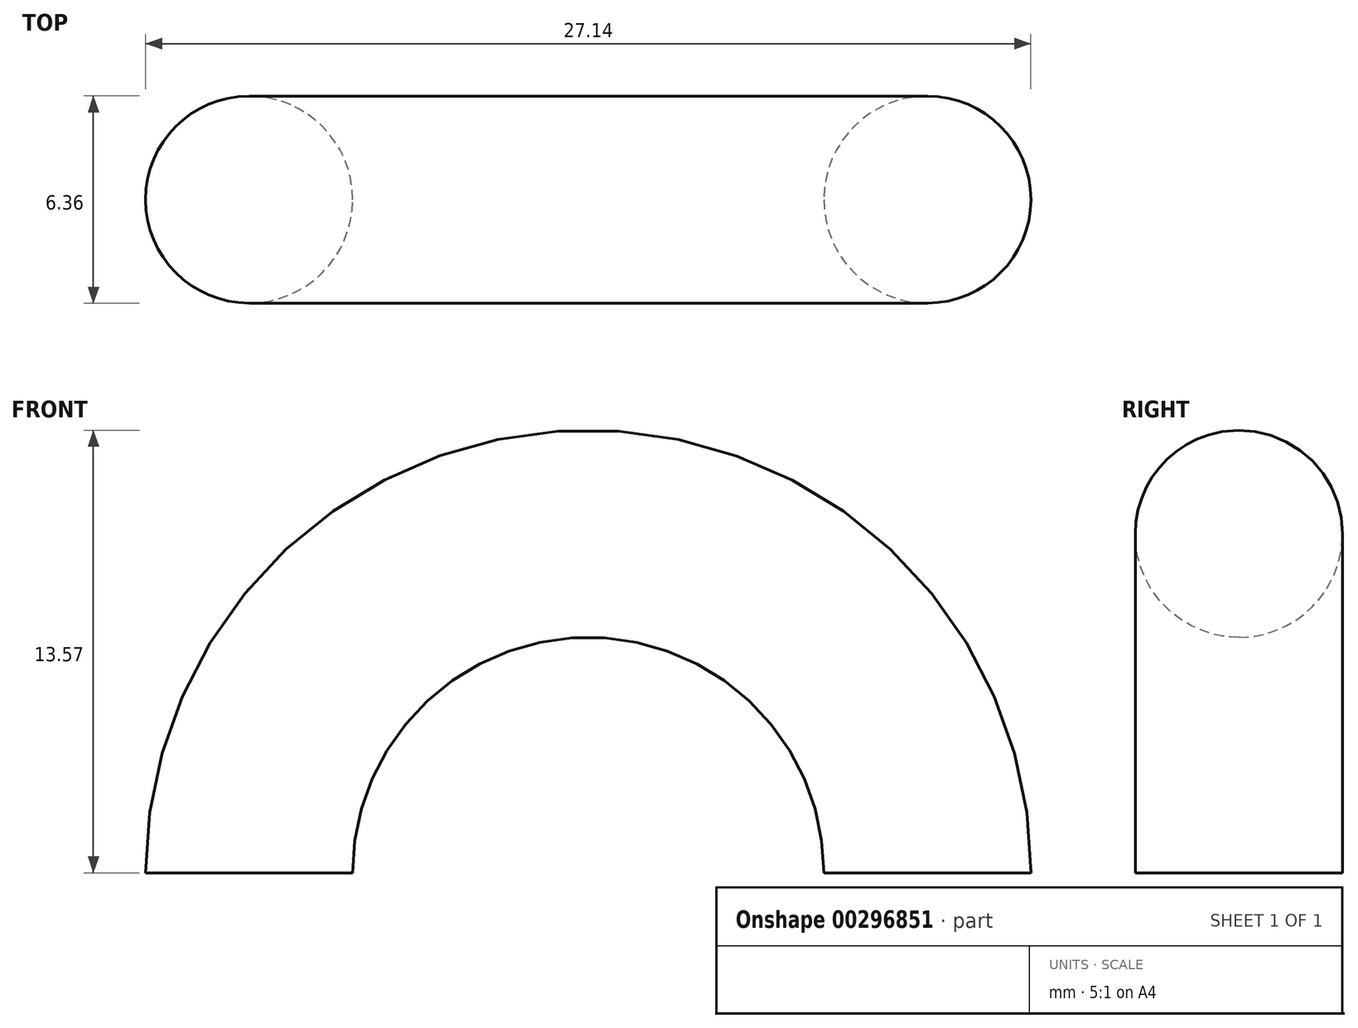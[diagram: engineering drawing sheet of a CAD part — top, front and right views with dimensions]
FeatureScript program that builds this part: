
annotation { "Feature Type Name" : "Feature", "Feature Type Description" : "" }
export const myFeature = defineFeature(function(context is Context, id is Id, definition is map)
    precondition{}
    {
        {
            var Q0;
            Q0=qCreatedBy(makeId("Top.planeOp"),FACE);
            var sketch = newSketch(context, id + "F0", { "sketchPlane" : qUnion([Q0])});
            skCircle(sketch, "E0", {"center": v(-10.4, 0) * mm, "radius": 3.18 * mm});
            skSolve(sketch);
        }
        {
            var Q0;
            Q0=qCreatedBy(makeId("Top.planeOp"),FACE);
            var sketch = newSketch(context, id + "F1", { "sketchPlane" : qUnion([Q0])});
            skLineSegment(sketch, "E1", {"start": v(0, -32.99) * mm, "end": v(0, 34.7) * mm});
            skSolve(sketch);
        }
        {
            var Q0;
            Q0=makeQuery(id+"F0.imprint","IMPRINT",FACE,{"disambiguationData":[TD([[makeQuery(id+"F0.imprint","IMPRINT",EDGE,{"derivedFrom":sQuery(id+"F0.wireOp",EDGE,"E0")}),1.0]])]});
            var Q1;
            Q1=sQuery(id+"F1.wireOp",EDGE,"E1");
            revolve(context, id + "F2", {"entities" : qUnion([Q0]), "axis" : qUnion([Q1]), "revolveType" : RevolveType.ONE_DIRECTION, "angle" : 180 * degree});
        }
    });
